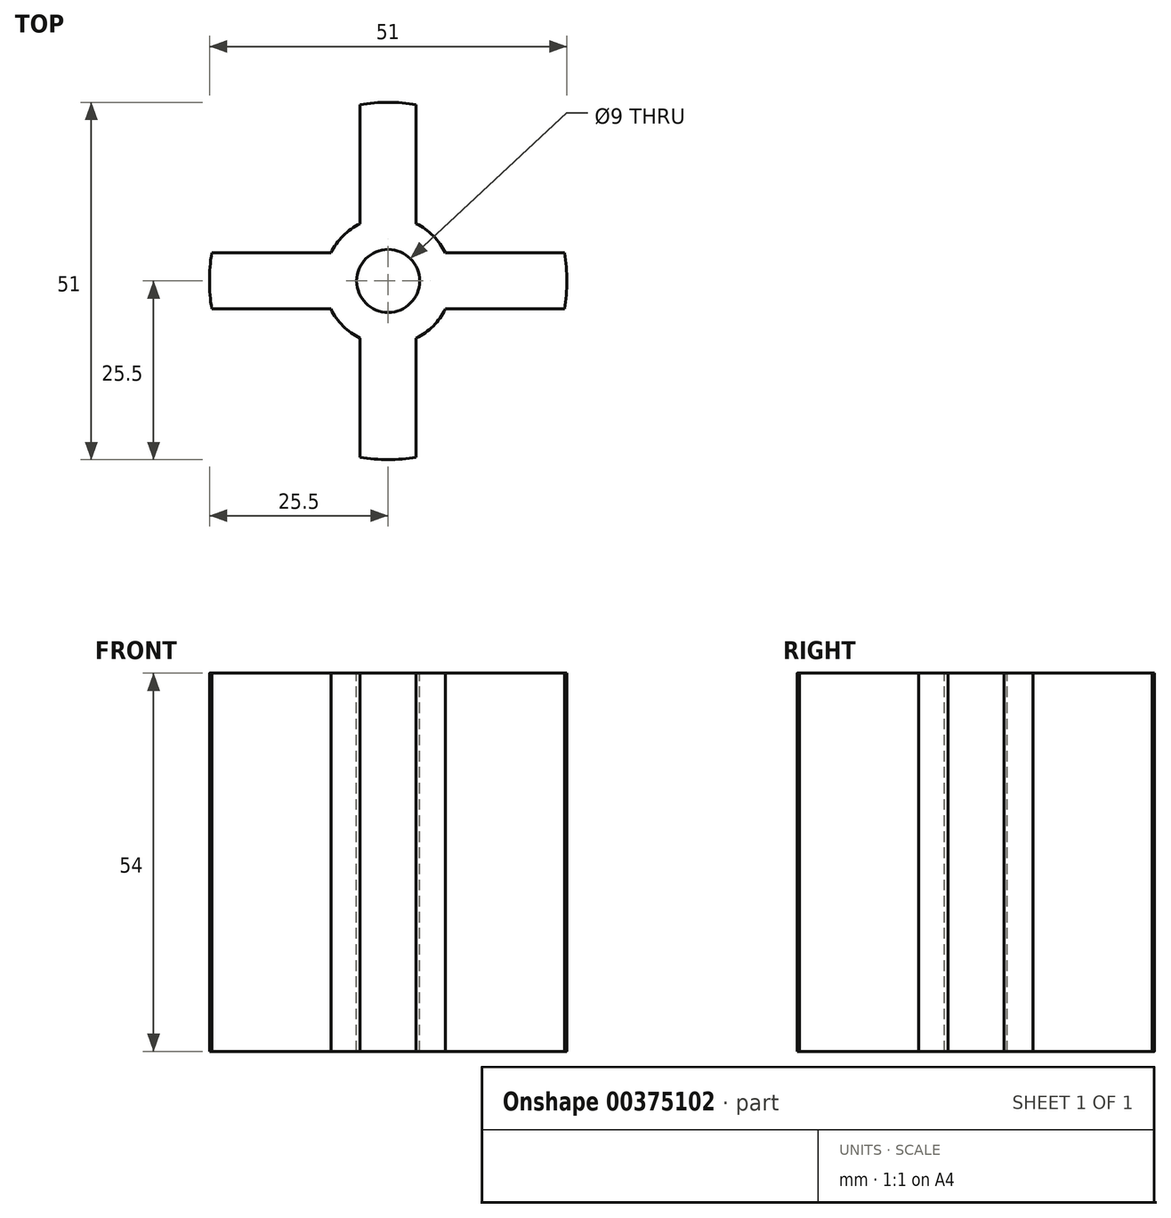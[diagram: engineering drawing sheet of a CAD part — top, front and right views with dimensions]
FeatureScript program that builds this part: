
annotation { "Feature Type Name" : "Feature", "Feature Type Description" : "" }
export const myFeature = defineFeature(function(context is Context, id is Id, definition is map)
    precondition{}
    {
        {
            var Q0;
            Q0=qCreatedBy(makeId("Top.planeOp"),FACE);
            var sketch = newSketch(context, id + "F0", { "sketchPlane" : qUnion([Q0])});
            skCircle(sketch, "E0", {"center": v(0, 0) * mm, "radius": 11.1 * mm});
            skCircle(sketch, "E1.0", {"center": v(0, 0) * mm, "radius": 13.1 * mm});
            skCircle(sketch, "E2.0", {"center": v(0, 0) * mm, "radius": 9.1 * mm});
            skCircle(sketch, "E3", {"center": v(0, 0) * mm, "radius": 25.5 * mm});
            skLineSegment(sketch, "E4.bottom", {"start": v(-4, -25.18) * mm, "end": v(4, -25.18) * mm});
            skLineSegment(sketch, "E4.top", {"start": v(-4, 25.18) * mm, "end": v(4, 25.18) * mm});
            skLineSegment(sketch, "E4.left", {"start": v(-4, -25.18) * mm, "end": v(-4, 25.18) * mm});
            skLineSegment(sketch, "E4.right", {"start": v(4, -25.18) * mm, "end": v(4, 25.18) * mm});
            skLineSegment(sketch, "E5.bottom", {"start": v(-25.18, -4) * mm, "end": v(25.18, -4) * mm});
            skLineSegment(sketch, "E5.top", {"start": v(-25.18, 4) * mm, "end": v(25.18, 4) * mm});
            skLineSegment(sketch, "E5.left", {"start": v(-25.18, -4) * mm, "end": v(-25.18, 4) * mm});
            skLineSegment(sketch, "E5.right", {"start": v(25.18, -4) * mm, "end": v(25.18, 4) * mm});
            skCircle(sketch, "E6", {"center": v(0, 0) * mm, "radius": 4.5 * mm});
            skSolve(sketch);
        }
        {
            var Q0;
            {var subQ5=sQuery(id+"F0.wireOp",EDGE,"E4.top");Q0=makeQuery(id+"F0.imprint","IMPRINT",FACE,{"disambiguationData":[TD([[makeQuery(id+"F0.imprint","IMPRINT",EDGE,{"derivedFrom":subQ5}),-1.0]])]});}
            var Q1;
            {var subQ0=sQuery(id+"F0.wireOp",EDGE,"E4.top");Q1=makeQuery(id+"F0.imprint","IMPRINT",FACE,{"disambiguationData":[TD([[makeQuery(id+"F0.imprint","IMPRINT",EDGE,{"derivedFrom":subQ0}),1.0]])]});}
            var Q2;
            {var subQ0=sQuery(id+"F0.wireOp",EDGE,"E5.right");Q2=makeQuery(id+"F0.imprint","IMPRINT",FACE,{"disambiguationData":[TD([[makeQuery(id+"F0.imprint","IMPRINT",EDGE,{"derivedFrom":subQ0}),-1.0]])]});}
            var Q3;
            {var subQ5=sQuery(id+"F0.wireOp",EDGE,"E5.right");Q3=makeQuery(id+"F0.imprint","IMPRINT",FACE,{"disambiguationData":[TD([[makeQuery(id+"F0.imprint","IMPRINT",EDGE,{"derivedFrom":subQ5}),1.0]])]});}
            var Q4;
            {var subQ0=sQuery(id+"F0.wireOp",EDGE,"E4.bottom");Q4=makeQuery(id+"F0.imprint","IMPRINT",FACE,{"disambiguationData":[TD([[makeQuery(id+"F0.imprint","IMPRINT",EDGE,{"derivedFrom":subQ0}),-1.0]])]});}
            var Q5;
            {var subQ0=sQuery(id+"F0.wireOp",EDGE,"E5.left");Q5=makeQuery(id+"F0.imprint","IMPRINT",FACE,{"disambiguationData":[TD([[makeQuery(id+"F0.imprint","IMPRINT",EDGE,{"derivedFrom":subQ0}),1.0]])]});}
            var Q6;
            {var subQ5=sQuery(id+"F0.wireOp",EDGE,"E5.left");Q6=makeQuery(id+"F0.imprint","IMPRINT",FACE,{"disambiguationData":[TD([[makeQuery(id+"F0.imprint","IMPRINT",EDGE,{"derivedFrom":subQ5}),-1.0]])]});}
            var Q7;
            {var subQ5=sQuery(id+"F0.wireOp",EDGE,"E4.bottom");Q7=makeQuery(id+"F0.imprint","IMPRINT",FACE,{"disambiguationData":[TD([[makeQuery(id+"F0.imprint","IMPRINT",EDGE,{"derivedFrom":subQ5}),1.0]])]});}
            var Q8;
            {var subQ0=sQuery(id+"F0.wireOp",EDGE,"E5.top");var subQ1=sQuery(id+"F0.wireOp",EDGE,"E0");var subQ2=makeQuery(id+"F0.imprint","INTERSECT",VERTEX,{"disambiguationData":[OD(1.0)],"derivedFrom":[subQ1,subQ0]});Q8=makeQuery(id+"F0.imprint","IMPRINT",FACE,{"disambiguationData":[TD([[makeQuery(id+"F0.imprint","IMPRINT",EDGE,{"disambiguationData":[TD([[subQ2,-1.0]])],"derivedFrom":subQ1}),1.0]])]});}
            var Q9;
            {var subQ0=sQuery(id+"F0.wireOp",EDGE,"E5.top");var subQ1=sQuery(id+"F0.wireOp",EDGE,"E0");var subQ2=makeQuery(id+"F0.imprint","INTERSECT",VERTEX,{"disambiguationData":[OD(1.0)],"derivedFrom":[subQ1,subQ0]});Q9=makeQuery(id+"F0.imprint","IMPRINT",FACE,{"disambiguationData":[TD([[makeQuery(id+"F0.imprint","IMPRINT",EDGE,{"disambiguationData":[TD([[subQ2,-1.0]])],"derivedFrom":subQ1}),-1.0]])]});}
            var Q10;
            {var subQ0=sQuery(id+"F0.wireOp",EDGE,"E4.right");var subQ1=sQuery(id+"F0.wireOp",EDGE,"E0");var subQ2=makeQuery(id+"F0.imprint","INTERSECT",VERTEX,{"disambiguationData":[OD(0.0)],"derivedFrom":[subQ1,subQ0]});Q10=makeQuery(id+"F0.imprint","IMPRINT",FACE,{"disambiguationData":[TD([[makeQuery(id+"F0.imprint","IMPRINT",EDGE,{"disambiguationData":[TD([[subQ2,-1.0]])],"derivedFrom":subQ1}),1.0]])]});}
            var Q11;
            {var subQ0=sQuery(id+"F0.wireOp",EDGE,"E4.right");var subQ1=sQuery(id+"F0.wireOp",EDGE,"E0");var subQ2=makeQuery(id+"F0.imprint","INTERSECT",VERTEX,{"disambiguationData":[OD(0.0)],"derivedFrom":[subQ1,subQ0]});Q11=makeQuery(id+"F0.imprint","IMPRINT",FACE,{"disambiguationData":[TD([[makeQuery(id+"F0.imprint","IMPRINT",EDGE,{"disambiguationData":[TD([[subQ2,-1.0]])],"derivedFrom":subQ1}),-1.0]])]});}
            var Q12;
            {var subQ0=sQuery(id+"F0.wireOp",EDGE,"E5.top");var subQ1=sQuery(id+"F0.wireOp",EDGE,"E0");var subQ2=makeQuery(id+"F0.imprint","INTERSECT",VERTEX,{"disambiguationData":[OD(0.0)],"derivedFrom":[subQ1,subQ0]});Q12=makeQuery(id+"F0.imprint","IMPRINT",FACE,{"disambiguationData":[TD([[makeQuery(id+"F0.imprint","IMPRINT",EDGE,{"disambiguationData":[TD([[subQ2,1.0]])],"derivedFrom":subQ1}),-1.0]])]});}
            var Q13;
            {var subQ0=sQuery(id+"F0.wireOp",EDGE,"E5.top");var subQ1=sQuery(id+"F0.wireOp",EDGE,"E0");var subQ2=makeQuery(id+"F0.imprint","INTERSECT",VERTEX,{"disambiguationData":[OD(0.0)],"derivedFrom":[subQ1,subQ0]});Q13=makeQuery(id+"F0.imprint","IMPRINT",FACE,{"disambiguationData":[TD([[makeQuery(id+"F0.imprint","IMPRINT",EDGE,{"disambiguationData":[TD([[subQ2,1.0]])],"derivedFrom":subQ1}),1.0]])]});}
            var Q14;
            {var subQ0=sQuery(id+"F0.wireOp",EDGE,"E4.left");var subQ1=sQuery(id+"F0.wireOp",EDGE,"E0");var subQ2=makeQuery(id+"F0.imprint","INTERSECT",VERTEX,{"disambiguationData":[OD(1.0)],"derivedFrom":[subQ1,subQ0]});Q14=makeQuery(id+"F0.imprint","IMPRINT",FACE,{"disambiguationData":[TD([[makeQuery(id+"F0.imprint","IMPRINT",EDGE,{"disambiguationData":[TD([[subQ2,-1.0]])],"derivedFrom":subQ1}),1.0]])]});}
            var Q15;
            {var subQ0=sQuery(id+"F0.wireOp",EDGE,"E4.left");var subQ1=sQuery(id+"F0.wireOp",EDGE,"E0");var subQ2=makeQuery(id+"F0.imprint","INTERSECT",VERTEX,{"disambiguationData":[OD(1.0)],"derivedFrom":[subQ1,subQ0]});Q15=makeQuery(id+"F0.imprint","IMPRINT",FACE,{"disambiguationData":[TD([[makeQuery(id+"F0.imprint","IMPRINT",EDGE,{"disambiguationData":[TD([[subQ2,-1.0]])],"derivedFrom":subQ1}),-1.0]])]});}
            var Q16;
            {var subQ3=sQuery(id+"F0.wireOp",EDGE,"E5.top");var subQ8=sQuery(id+"F0.wireOp",EDGE,"E2.0");var subQ10=makeQuery(id+"F0.imprint","INTERSECT",VERTEX,{"disambiguationData":[OD(1.0)],"derivedFrom":[subQ8,subQ3]});Q16=makeQuery(id+"F0.imprint","IMPRINT",FACE,{"disambiguationData":[TD([[makeQuery(id+"F0.imprint","IMPRINT",EDGE,{"disambiguationData":[TD([[subQ10,-1.0]])],"derivedFrom":subQ8}),1.0]])]});}
            var Q17;
            {var subQ0=sQuery(id+"F0.wireOp",EDGE,"E4.left");var subQ1=sQuery(id+"F0.wireOp",EDGE,"E2.0");var subQ2=makeQuery(id+"F0.imprint","INTERSECT",VERTEX,{"disambiguationData":[OD(0.0)],"derivedFrom":[subQ1,subQ0]});Q17=makeQuery(id+"F0.imprint","IMPRINT",FACE,{"disambiguationData":[TD([[makeQuery(id+"F0.imprint","IMPRINT",EDGE,{"disambiguationData":[TD([[subQ2,-1.0]])],"derivedFrom":subQ1}),1.0]])]});}
            var Q18;
            {var subQ5=sQuery(id+"F0.wireOp",EDGE,"E2.0");var subQ7=sQuery(id+"F0.wireOp",EDGE,"E4.right");var subQ8=makeQuery(id+"F0.imprint","INTERSECT",VERTEX,{"disambiguationData":[OD(0.0)],"derivedFrom":[subQ5,subQ7]});Q18=makeQuery(id+"F0.imprint","IMPRINT",FACE,{"disambiguationData":[TD([[makeQuery(id+"F0.imprint","IMPRINT",EDGE,{"disambiguationData":[TD([[subQ8,-1.0]])],"derivedFrom":subQ5}),1.0]])]});}
            var Q19;
            {var subQ0=sQuery(id+"F0.wireOp",EDGE,"E4.right");var subQ1=sQuery(id+"F0.wireOp",EDGE,"E2.0");var subQ2=makeQuery(id+"F0.imprint","INTERSECT",VERTEX,{"disambiguationData":[OD(0.0)],"derivedFrom":[subQ1,subQ0]});Q19=makeQuery(id+"F0.imprint","IMPRINT",FACE,{"disambiguationData":[TD([[makeQuery(id+"F0.imprint","IMPRINT",EDGE,{"disambiguationData":[TD([[subQ2,1.0]])],"derivedFrom":subQ1}),1.0]])]});}
            var Q20;
            {var subQ3=sQuery(id+"F0.wireOp",EDGE,"E5.top");var subQ8=sQuery(id+"F0.wireOp",EDGE,"E2.0");var subQ10=makeQuery(id+"F0.imprint","INTERSECT",VERTEX,{"disambiguationData":[OD(0.0)],"derivedFrom":[subQ8,subQ3]});Q20=makeQuery(id+"F0.imprint","IMPRINT",FACE,{"disambiguationData":[TD([[makeQuery(id+"F0.imprint","IMPRINT",EDGE,{"disambiguationData":[TD([[subQ10,1.0]])],"derivedFrom":subQ8}),1.0]])]});}
            var Q21;
            {var subQ1=sQuery(id+"F0.wireOp",EDGE,"E4.left");var subQ6=sQuery(id+"F0.wireOp",EDGE,"E2.0");var subQ9=makeQuery(id+"F0.imprint","INTERSECT",VERTEX,{"disambiguationData":[OD(1.0)],"derivedFrom":[subQ6,subQ1]});Q21=makeQuery(id+"F0.imprint","IMPRINT",FACE,{"disambiguationData":[TD([[makeQuery(id+"F0.imprint","IMPRINT",EDGE,{"disambiguationData":[TD([[subQ9,-1.0]])],"derivedFrom":subQ6}),1.0]])]});}
            var Q22;
            {var subQ0=sQuery(id+"F0.wireOp",EDGE,"E5.bottom");var subQ1=sQuery(id+"F0.wireOp",EDGE,"E2.0");var subQ2=makeQuery(id+"F0.imprint","INTERSECT",VERTEX,{"disambiguationData":[OD(0.0)],"derivedFrom":[subQ1,subQ0]});Q22=makeQuery(id+"F0.imprint","IMPRINT",FACE,{"disambiguationData":[TD([[makeQuery(id+"F0.imprint","IMPRINT",EDGE,{"disambiguationData":[TD([[subQ2,-1.0]])],"derivedFrom":subQ1}),1.0]])]});}
            var Q23;
            {var subQ0=sQuery(id+"F0.wireOp",EDGE,"E4.right");var subQ1=sQuery(id+"F0.wireOp",EDGE,"E2.0");var subQ2=makeQuery(id+"F0.imprint","INTERSECT",VERTEX,{"disambiguationData":[OD(1.0)],"derivedFrom":[subQ1,subQ0]});Q23=makeQuery(id+"F0.imprint","IMPRINT",FACE,{"disambiguationData":[TD([[makeQuery(id+"F0.imprint","IMPRINT",EDGE,{"disambiguationData":[TD([[subQ2,-1.0]])],"derivedFrom":subQ1}),1.0]])]});}
            var Q24;
            {var subQ0=sQuery(id+"F0.wireOp",EDGE,"E5.bottom");var subQ1=sQuery(id+"F0.wireOp",EDGE,"E4.right");var subQ2=makeQuery(id+"F0.imprint","INTERSECT",VERTEX,{"derivedFrom":[subQ1,subQ0]});Q24=makeQuery(id+"F0.imprint","IMPRINT",FACE,{"disambiguationData":[TD([[makeQuery(id+"F0.imprint","IMPRINT",EDGE,{"disambiguationData":[TD([[subQ2,-1.0]])],"derivedFrom":subQ1}),1.0]])]});}
            var Q25;
            {var subQ0=sQuery(id+"F0.wireOp",EDGE,"E5.bottom");var subQ1=sQuery(id+"F0.wireOp",EDGE,"E4.left");var subQ2=makeQuery(id+"F0.imprint","INTERSECT",VERTEX,{"derivedFrom":[subQ1,subQ0]});Q25=makeQuery(id+"F0.imprint","IMPRINT",FACE,{"disambiguationData":[TD([[makeQuery(id+"F0.imprint","IMPRINT",EDGE,{"disambiguationData":[TD([[subQ2,-1.0]])],"derivedFrom":subQ1}),-1.0]])]});}
            var Q26;
            {var subQ0=sQuery(id+"F0.wireOp",EDGE,"E6");var subQ1=sQuery(id+"F0.wireOp",EDGE,"E4.left");var subQ2=makeQuery(id+"F0.imprint","INTERSECT",VERTEX,{"disambiguationData":[OD(1.0)],"derivedFrom":[subQ1,subQ0]});Q26=makeQuery(id+"F0.imprint","IMPRINT",FACE,{"disambiguationData":[TD([[makeQuery(id+"F0.imprint","IMPRINT",EDGE,{"disambiguationData":[TD([[subQ2,-1.0]])],"derivedFrom":subQ1}),-1.0]])]});}
            var Q27;
            {var subQ0=sQuery(id+"F0.wireOp",EDGE,"E6");var subQ1=sQuery(id+"F0.wireOp",EDGE,"E4.right");var subQ2=makeQuery(id+"F0.imprint","INTERSECT",VERTEX,{"disambiguationData":[OD(1.0)],"derivedFrom":[subQ1,subQ0]});Q27=makeQuery(id+"F0.imprint","IMPRINT",FACE,{"disambiguationData":[TD([[makeQuery(id+"F0.imprint","IMPRINT",EDGE,{"disambiguationData":[TD([[subQ2,-1.0]])],"derivedFrom":subQ1}),1.0]])]});}
            extrude(context, id + "F1", {"entities" : qUnion([Q0, Q1, Q2, Q3, Q4, Q5, Q6, Q7, Q8, Q9, Q10, Q11, Q12, Q13, Q14, Q15, Q16, Q17, Q18, Q19, Q20, Q21, Q22, Q23, Q24, Q25, Q26, Q27]), "oppositeDirection" : true, "depth" : 54 * mm});
        }
    });
